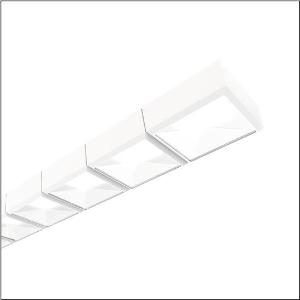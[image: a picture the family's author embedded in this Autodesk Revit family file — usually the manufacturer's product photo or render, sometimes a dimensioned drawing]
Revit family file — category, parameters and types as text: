
# Revit family: scriptus_r__11_5mz313d04wa_45ce
name_source: partatom
category: Lighting Fixtures
units: mm (PartAtom-declared; Revit-internal decimal feet)

## family parameters
Cut with Voids When Loaded = No
Host = Face
Light Source = No
Part Type = Normal
Room Calculation Point = No
Round Connector Dimension = Use Diameter
Shared = No

## types (1)
- Scriptus® 11 (1 x LED 4000K / CRI = 80 (unbekannt), 2660 lm / 4010 lm, 4000K)
    Apparent Load = 99 VA
    CIE Flux Codes = - - - 0 100 / 82 95 99 100 100
    Color Rendering = 80
    Color Temperature = 4000K
    Default Elevation = 1800 mm
    Description = Scriptus® 11, office luminaire, primary optical cover: lenses, CAT 2 (L<= 3000cd/m²), light emission: direct/indirect distribution, primary light characteristic: symmetric, installation type: suspended mounting, LED, rated luminous flux: 13.330lm, luminous efficacy: 134lm/W, light colour: 840, colour temperature: 4000K, control gear: ECG DALI, with terminal, 5-pole, mains connection: 230V, AC, 50Hz, rated input power: 99W, LED, control gear: ECG DALI, housing, luminaire housing, of aluminium, traffic white (RAL 9016), length: 2.648mm, width: 114mm, height: 57mm, protection rating (complete): IP20, insulation class (complete): insulation class I (protective earthing), certification: CE, ENEC, VDE, protection symbol: F, permissible operating ambient temperature: 0..+35°C, standard: EN 50419, packaging unit: 1 piece
    Height = 57 mm
    Lamp = 1 x LED 4000K / CRI >= 80 (unbekannt)
    Lamp Light Flux = 2660 lm / 4010 lm
    Lamp count = 1
    Length = 2648 mm
    Luminous efficacy = 134 lm/W
    Manufacturer = Siteco
    ModVariant = No
    Model = 5MZ313D04WA
    Mounting Place = Ceiling
    Mounting Type = Pendant
    Number of Poles = 1
    OnlyDefault = Yes
    Power Factor = 1
    Product Name = Scriptus® 11
    Product group = office luminaire | ceiling pendant
    ProductGroupID = 902
    Protection Class = Protection class I
    Protection Degree = IP 20
    RLX_Detail_Level = 1
    RLX_Emergency_Light_Flux = 0 lm
    RLX_Emergency_Type = 0
    RLX_Emergency_Type_DB = No
    RlxData = <blob elided: 31617 chars, md5=6317bf6e>
    Socket = socket
    Standby Power = 0 W
    System Light Flux = 13340 lm
    System Power = 99 W
    Type Comments = Product without accessories
    Type Image = l_1004839.jpg
    URL = http://relux.com
    VarID = ---
    Voltage = 0 V
    Weight = 0.00 kg
    Width = 114 mm

## geometry (parser evidence)
native form markers: Blend x4, Sweep x20
no freeform markers — native parametric forms only
